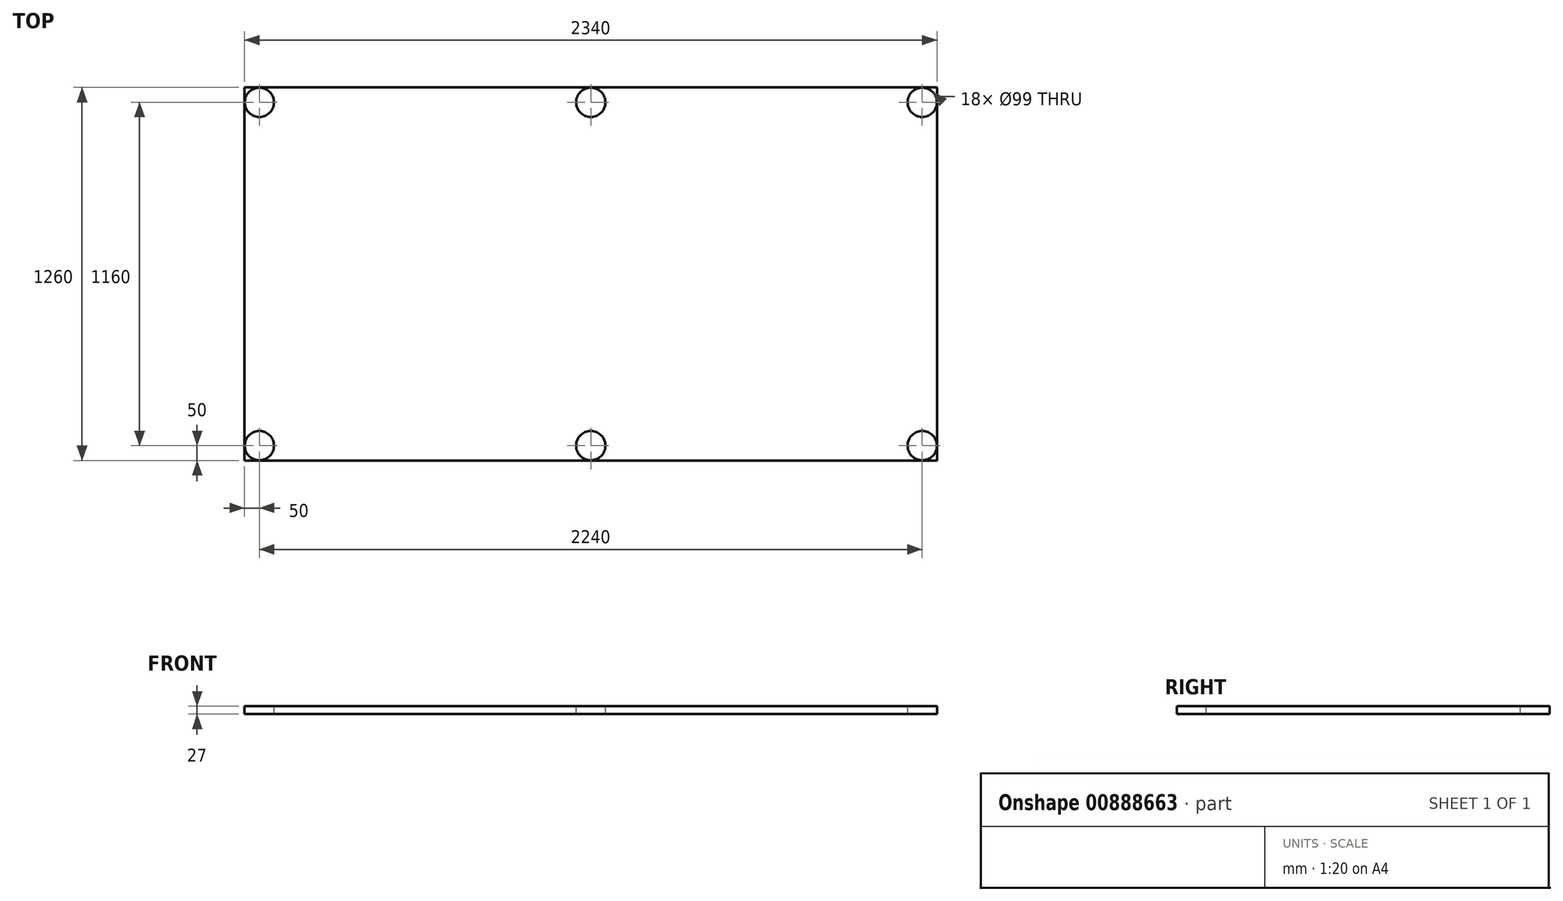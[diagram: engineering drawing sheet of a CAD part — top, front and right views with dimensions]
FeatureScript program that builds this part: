
annotation { "Feature Type Name" : "Feature", "Feature Type Description" : "" }
export const myFeature = defineFeature(function(context is Context, id is Id, definition is map)
    precondition{}
    {
        {
            var Q0;
            Q0=qCreatedBy(makeId("Top.planeOp"),FACE);
            var sketch = newSketch(context, id + "F0", { "sketchPlane" : qUnion([Q0])});
            skLineSegment(sketch, "E0.bottom", {"start": v(0, 0) * mm, "end": v(2340, 0) * mm});
            skLineSegment(sketch, "E0.top", {"start": v(0, 1260) * mm, "end": v(2340, 1260) * mm});
            skLineSegment(sketch, "E0.left", {"start": v(0, 0) * mm, "end": v(0, 1260) * mm});
            skLineSegment(sketch, "E0.right", {"start": v(2340, 0) * mm, "end": v(2340, 1260) * mm});
            skSolve(sketch);
        }
        {
            var Q0;
            Q0 = qSketchRegion(id + "F0", true);
            extrude(context, id + "F1", {"entities" : qUnion([Q0]), "depth" : 27 * mm, "offsetDistance" : 25 * mm});
        }
        {
            var Q0;
            Q0=makeQuery(id+"F1.opExtrude","CAP_FACE",FACE,{"disambiguationData":[OSD([sQuery(id+"F0.wireOp",EDGE,"E0.bottom"),sQuery(id+"F0.wireOp",EDGE,"E0.top"),sQuery(id+"F0.wireOp",EDGE,"E0.left"),sQuery(id+"F0.wireOp",EDGE,"E0.right")])],"isStart":false});
            var sketch = newSketch(context, id + "F2", { "sketchPlane" : qUnion([Q0])});
            skCircle(sketch, "E1", {"center": v(50, 50) * mm, "radius": 49.5 * mm});
            skCircle(sketch, "E2", {"center": v(50, 1210) * mm, "radius": 49.5 * mm});
            skCircle(sketch, "E3", {"center": v(1170, 1210) * mm, "radius": 49.5 * mm});
            skCircle(sketch, "E4", {"center": v(2290, 1210) * mm, "radius": 49.5 * mm});
            skCircle(sketch, "E5", {"center": v(2290, 50) * mm, "radius": 49.5 * mm});
            skCircle(sketch, "E6", {"center": v(1170, 50) * mm, "radius": 49.5 * mm});
            skSolve(sketch);
        }
        {
            var Q0;
            Q0=makeQuery(id+"F2.imprint","IMPRINT",FACE,{"disambiguationData":[TD([[makeQuery(id+"F2.imprint","IMPRINT",EDGE,{"derivedFrom":sQuery(id+"F2.wireOp",EDGE,"E2")}),1.0]])]});
            var Q1;
            Q1=makeQuery(id+"F2.imprint","IMPRINT",FACE,{"disambiguationData":[TD([[makeQuery(id+"F2.imprint","IMPRINT",EDGE,{"derivedFrom":sQuery(id+"F2.wireOp",EDGE,"E3")}),1.0]])]});
            var Q2;
            Q2=makeQuery(id+"F2.imprint","IMPRINT",FACE,{"disambiguationData":[TD([[makeQuery(id+"F2.imprint","IMPRINT",EDGE,{"derivedFrom":sQuery(id+"F2.wireOp",EDGE,"E4")}),1.0]])]});
            var Q3;
            Q3=makeQuery(id+"F2.imprint","IMPRINT",FACE,{"disambiguationData":[TD([[makeQuery(id+"F2.imprint","IMPRINT",EDGE,{"derivedFrom":sQuery(id+"F2.wireOp",EDGE,"E5")}),1.0]])]});
            var Q4;
            Q4=makeQuery(id+"F2.imprint","IMPRINT",FACE,{"disambiguationData":[TD([[makeQuery(id+"F2.imprint","IMPRINT",EDGE,{"derivedFrom":sQuery(id+"F2.wireOp",EDGE,"E6")}),1.0]])]});
            var Q5;
            Q5=makeQuery(id+"F2.imprint","IMPRINT",FACE,{"disambiguationData":[TD([[makeQuery(id+"F2.imprint","IMPRINT",EDGE,{"derivedFrom":sQuery(id+"F2.wireOp",EDGE,"E1")}),1.0]])]});
            extrude(context, id + "F3", {"entities" : qUnion([Q0, Q1, Q2, Q3, Q4, Q5]), "operationType" : NewBodyOperationType.REMOVE, "endBound" : BoundingType.THROUGH_ALL, "oppositeDirection" : true, "depth" : 25 * mm, "offsetDistance" : 25 * mm});
        }
    });
